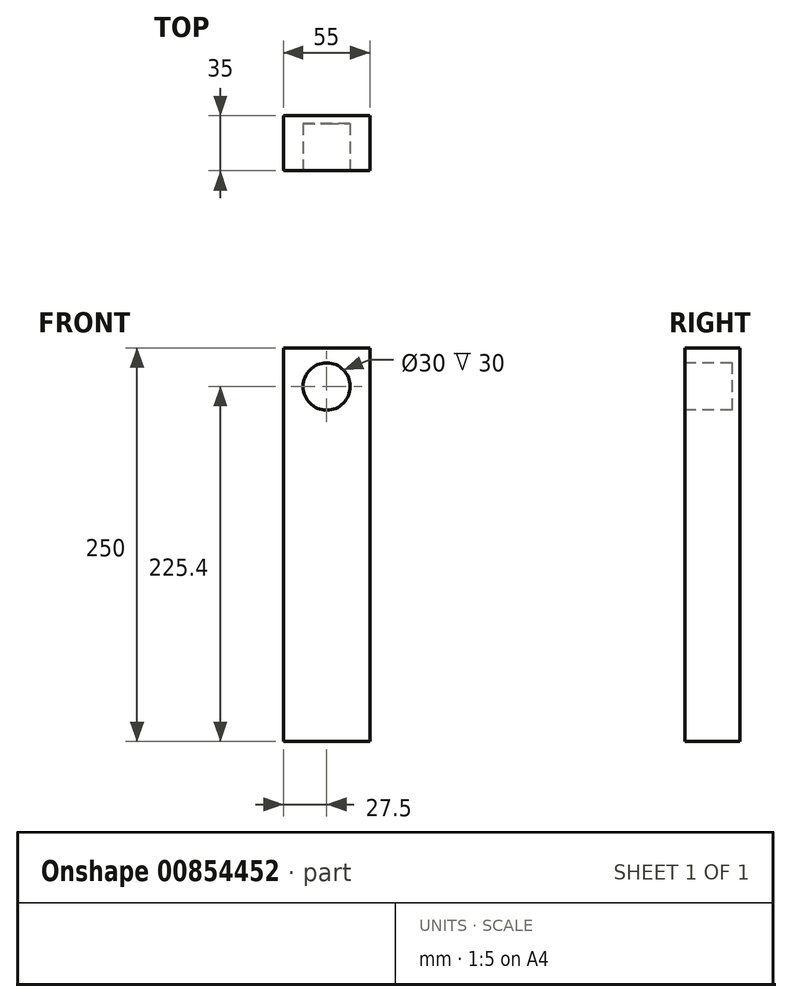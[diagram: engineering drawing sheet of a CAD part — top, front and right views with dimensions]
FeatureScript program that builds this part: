
annotation { "Feature Type Name" : "Feature", "Feature Type Description" : "" }
export const myFeature = defineFeature(function(context is Context, id is Id, definition is map)
    precondition{}
    {
        {
            var Q0;
            Q0=qCreatedBy(makeId("Top.planeOp"),FACE);
            var sketch = newSketch(context, id + "F0", { "sketchPlane" : qUnion([Q0])});
            skLineSegment(sketch, "E0.bottom", {"start": v(-22.5, 17.5) * mm, "end": v(32.5, 17.5) * mm});
            skLineSegment(sketch, "E0.top", {"start": v(-22.5, -17.5) * mm, "end": v(32.5, -17.5) * mm});
            skLineSegment(sketch, "E0.left", {"start": v(-22.5, 17.5) * mm, "end": v(-22.5, -17.5) * mm});
            skLineSegment(sketch, "E0.right", {"start": v(32.5, 17.5) * mm, "end": v(32.5, -17.5) * mm});
            skSolve(sketch);
        }
        {
            var Q0;
            Q0=makeQuery(id+"F0.imprint","IMPRINT",FACE,{"disambiguationData":[TD([[makeQuery(id+"F0.imprint","IMPRINT",EDGE,{"derivedFrom":sQuery(id+"F0.wireOp",EDGE,"E0.bottom")}),-1.0]])]});
            extrude(context, id + "F1", {"entities" : qUnion([Q0]), "depth" : 250 * mm, "offsetDistance" : 25 * mm});
        }
        {
            var Q0;
            Q0=makeQuery(id+"F1.opExtrude","SWEPT_FACE",FACE,{"disambiguationData":[OSD([sQuery(id+"F0.wireOp",EDGE,"E0.top")])]});
            var sketch = newSketch(context, id + "F2", { "sketchPlane" : qUnion([Q0])});
            skCircle(sketch, "E1", {"center": v(5, 225.4) * mm, "radius": 15 * mm});
            skPoint(sketch, "E1.centerSnap0", {"position": v(5, 250) * mm});
            skSolve(sketch);
        }
        {
            var Q0;
            Q0=makeQuery(id+"F2.imprint","IMPRINT",FACE,{"disambiguationData":[TD([[makeQuery(id+"F2.imprint","IMPRINT",EDGE,{"derivedFrom":sQuery(id+"F2.wireOp",EDGE,"E1")}),1.0]])]});
            extrude(context, id + "F3", {"entities" : qUnion([Q0]), "operationType" : NewBodyOperationType.REMOVE, "oppositeDirection" : true, "depth" : 30 * mm, "offsetDistance" : 25 * mm});
        }
    });
